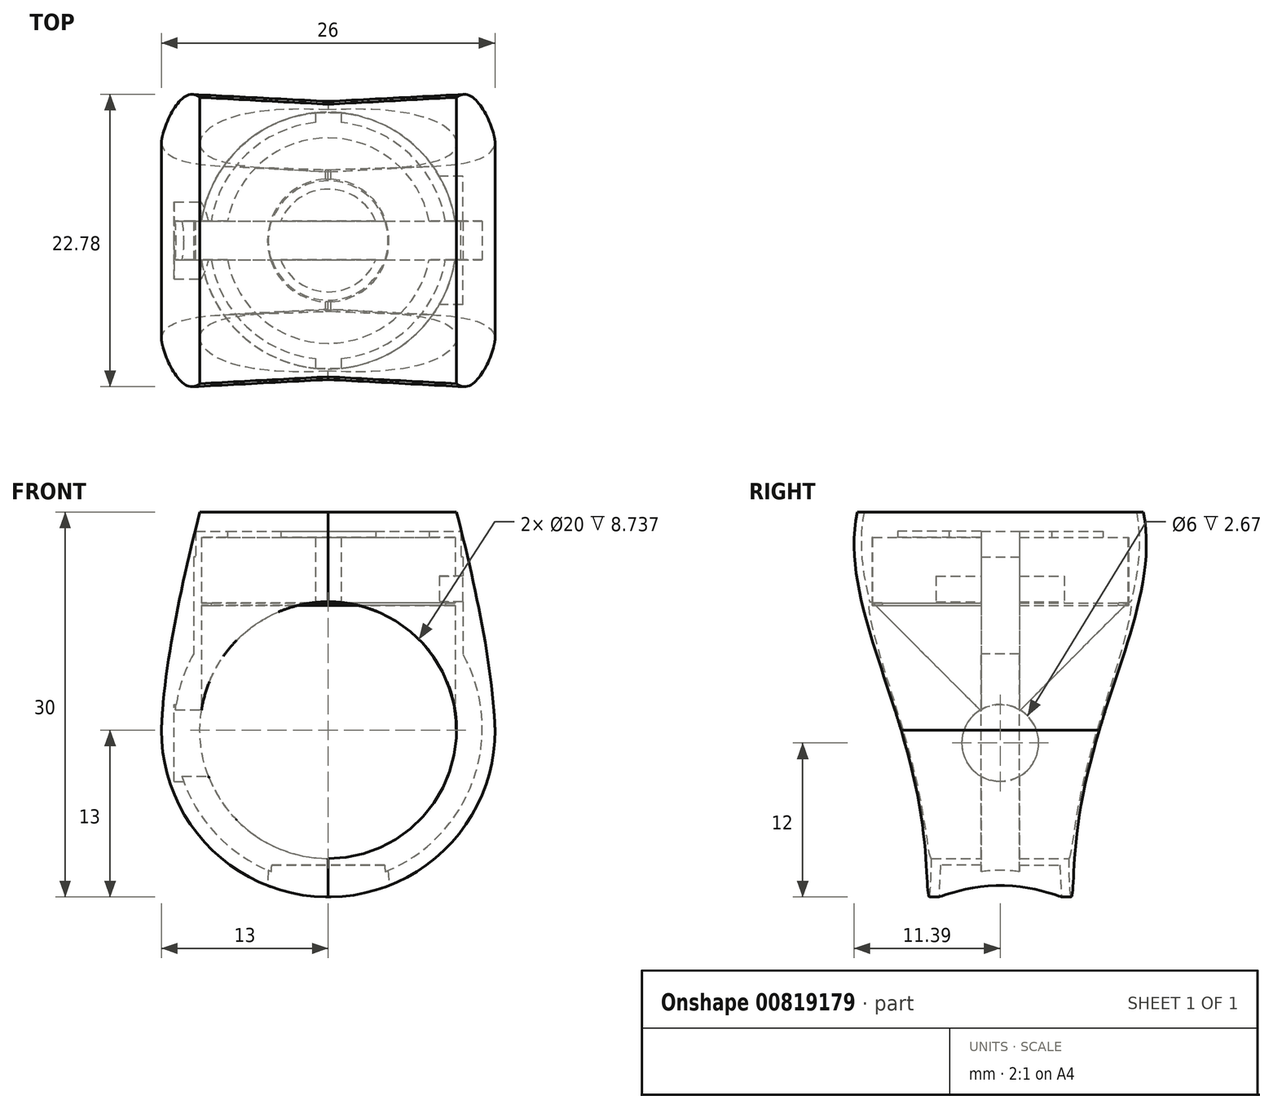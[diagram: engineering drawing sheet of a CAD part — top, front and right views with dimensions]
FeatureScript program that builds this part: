
annotation { "Feature Type Name" : "Feature", "Feature Type Description" : "" }
export const myFeature = defineFeature(function(context is Context, id is Id, definition is map)
    precondition{}
    {
        {
            var Q0;
            Q0=qCreatedBy(makeId("Front.planeOp"),FACE);
            var sketch = newSketch(context, id + "F0", { "sketchPlane" : qUnion([Q0])});
            skCircle(sketch, "E0", {"center": v(0, 0) * mm, "radius": 10 * mm});
            skLineSegment(sketch, "E1.bottom", {"start": v(-10, 11) * mm, "end": v(10, 11) * mm});
            skLineSegment(sketch, "E1.top", {"start": v(-10, 17) * mm, "end": v(10, 17) * mm});
            skLineSegment(sketch, "E1.left", {"start": v(-10, 11) * mm, "end": v(-10, 17) * mm});
            skLineSegment(sketch, "E1.right", {"start": v(10, 11) * mm, "end": v(10, 17) * mm});
            skPoint(sketch, "E1.middle", {"position": v(0, 14) * mm});
            skCircle(sketch, "E2.0", {"center": v(0, 0) * mm, "radius": 13 * mm});
            skPoint(sketch, "E3", {"position": v(0, 17) * mm});
            skPoint(sketch, "E4", {"position": v(0, 10) * mm});
            skFitSpline(sketch, "E5", {"points": [v(-10, 17) * mm, v(-13, 0) * mm], "startDerivative": vector(-4.4, -17) * mm, "endDerivative": vector(-0.5, -14.41) * mm});
            skFitSpline(sketch, "E6", {"points": [v(10, 17) * mm, v(13, 0) * mm], "startDerivative": vector(4.4, -17) * mm, "endDerivative": vector(0.5, -14.41) * mm});
            skSolve(sketch);
        }
        {
            var Q0;
            Q0=makeQuery(id+"F0.imprint","IMPRINT",FACE,{"disambiguationData":[TD([[makeQuery(id+"F0.imprint","IMPRINT",EDGE,{"derivedFrom":sQuery(id+"F0.wireOp",EDGE,"E0")}),-1.0]])]});
            var Q1;
            {var subQ0=sQuery(id+"F0.wireOp",EDGE,"E1.left");Q1=makeQuery(id+"F0.imprint","IMPRINT",FACE,{"disambiguationData":[TD([[makeQuery(id+"F0.imprint","IMPRINT",EDGE,{"derivedFrom":subQ0}),1.0]])]});}
            var Q2;
            {var subQ0=sQuery(id+"F0.wireOp",EDGE,"E1.right");Q2=makeQuery(id+"F0.imprint","IMPRINT",FACE,{"disambiguationData":[TD([[makeQuery(id+"F0.imprint","IMPRINT",EDGE,{"derivedFrom":subQ0}),-1.0]])]});}
            var Q3;
            {var subQ0=sQuery(id+"F0.wireOp",EDGE,"E2.0");var subQ1=sQuery(id+"F0.wireOp",EDGE,"E1.bottom");var subQ2=makeQuery(id+"F0.imprint","INTERSECT",VERTEX,{"disambiguationData":[OD(0.0)],"derivedFrom":[subQ1,subQ0]});Q3=makeQuery(id+"F0.imprint","IMPRINT",FACE,{"disambiguationData":[TD([[makeQuery(id+"F0.imprint","IMPRINT",EDGE,{"disambiguationData":[TD([[subQ2,-1.0]])],"derivedFrom":subQ1}),1.0]])]});}
            var Q4;
            Q4=makeQuery(id+"F0.imprint","IMPRINT",FACE,{"disambiguationData":[TD([[makeQuery(id+"F0.imprint","IMPRINT",EDGE,{"derivedFrom":sQuery(id+"F0.wireOp",EDGE,"E1.top")}),-1.0]])]});
            extrude(context, id + "F1", {"entities" : qUnion([Q0, Q1, Q2, Q3, Q4]), "depth" : 24.5 * mm, "offsetDistance" : 25 * mm, "symmetric" : true});
        }
        {
            var Q0;
            Q0=qCreatedBy(makeId("Right.planeOp"),FACE);
            var sketch = newSketch(context, id + "F2", { "sketchPlane" : qUnion([Q0])});
            skFitSpline(sketch, "E7", {"points": [v(-10.5, 17.51) * mm, v(-5.5, -12.99) * mm], "startDerivative": vector(-6.24, -25.28) * mm, "endDerivative": vector(-3.92, -38.96) * mm});
            skFitSpline(sketch, "E8", {"points": [v(10.5, 17.51) * mm, v(5.5, -12.99) * mm], "startDerivative": vector(6.24, -25.28) * mm, "endDerivative": vector(3.92, -38.96) * mm});
            skLineSegment(sketch, "E9", {"start": v(-5.5, -12.99) * mm, "end": v(5.5, -12.99) * mm});
            skLineSegment(sketch, "E10", {"start": v(-10.5, 17.51) * mm, "end": v(10.5, 17.51) * mm});
            skSolve(sketch);
        }
        {
            var Q0;
            Q0=qCreatedBy(makeId("Top.planeOp"),FACE);
            var sketch = newSketch(context, id + "F3", { "sketchPlane" : qUnion([Q0])});
            skPoint(sketch, "E11", {"position": v(0, 0) * mm});
            skCircle(sketch, "E12", {"center": v(0, 0) * mm, "radius": 10 * mm});
            skSolve(sketch);
        }
        {
            var Q0;
            Q0 = qSketchRegion(id + "F2", true);
            extrude(context, id + "F4", {"entities" : qUnion([Q0]), "operationType" : NewBodyOperationType.INTERSECT, "oppositeDirection" : true, "depth" : 80 * mm, "offsetDistance" : 25 * mm, "hasDraft" : true, "draftAngle" : 3 * degree, "symmetric" : true});
        }
        {
            var Q0;
            Q0 = qSketchRegion(id + "F3", true);
            var Q1;
            Q1 = qSketchRegion(id + "F12", true);
            extrude(context, id + "F5", {"entities" : qUnion([Q0, Q1]), "operationType" : NewBodyOperationType.REMOVE, "depth" : 15 * mm, "offsetDistance" : 25 * mm});
        }
        {
            var Q0;
            Q0=qCreatedBy(makeId("Top.planeOp"),FACE);
            var sketch = newSketch(context, id + "F6", { "sketchPlane" : qUnion([Q0])});
            skCircle(sketch, "E13", {"center": v(0, 0) * mm, "radius": 4.1 * mm});
            skSolve(sketch);
        }
        {
            var Q0;
            Q0 = qSketchRegion(id + "F6", true);
            extrude(context, id + "F7", {"entities" : qUnion([Q0]), "operationType" : NewBodyOperationType.REMOVE, "oppositeDirection" : true, "depth" : 14.4 * mm, "offsetDistance" : 44 * mm, "hasDraft" : true, "draftAngle" : 3 * degree, "hasSecondDirection" : true, "secondDirectionOppositeDirection" : true, "secondDirectionDepth" : 10.5 * mm});
        }
        {
            var Q0;
            Q0=qCreatedBy(makeId("Front.planeOp"),FACE);
            var sketch = newSketch(context, id + "F8", { "sketchPlane" : qUnion([Q0])});
            skCircle(sketch, "E14", {"center": v(0, 0.13) * mm, "radius": 12 * mm});
            skSolve(sketch);
        }
        {
            var Q0;
            Q0 = qSketchRegion(id + "F8", true);
            extrude(context, id + "F9", {"entities" : qUnion([Q0]), "operationType" : NewBodyOperationType.REMOVE, "oppositeDirection" : true, "depth" : 3 * mm, "offsetDistance" : 25 * mm, "symmetric" : true});
        }
        {
            var Q0;
            Q0=qCreatedBy(makeId("Right.planeOp"),FACE);
            var sketch = newSketch(context, id + "F10", { "sketchPlane" : qUnion([Q0])});
            skLineSegment(sketch, "E15.bottom", {"start": v(-1.5, 12.05) * mm, "end": v(1.5, 12.05) * mm});
            skLineSegment(sketch, "E15.top", {"start": v(-1.5, 3.05) * mm, "end": v(1.5, 3.05) * mm});
            skLineSegment(sketch, "E15.left", {"start": v(-1.5, 12.05) * mm, "end": v(-1.5, 3.05) * mm});
            skLineSegment(sketch, "E15.right", {"start": v(1.5, 12.05) * mm, "end": v(1.5, 3.05) * mm});
            skPoint(sketch, "E15.middle", {"position": v(0, 7.55) * mm});
            skSolve(sketch);
        }
        {
            var Q0;
            Q0 = qSketchRegion(id + "F10", true);
            var Q1;
            Q1 = qSketchRegion(id + "F12", true);
            extrude(context, id + "F11", {"entities" : qUnion([Q0, Q1]), "operationType" : NewBodyOperationType.REMOVE, "oppositeDirection" : true, "depth" : 21 * mm, "offsetDistance" : 25 * mm, "symmetric" : true});
        }
        {
            var Q0;
            Q0=qCreatedBy(makeId("Top.planeOp"),FACE);
            var sketch = newSketch(context, id + "F12", { "sketchPlane" : qUnion([Q0])});
            skCircle(sketch, "E16", {"center": v(0, 0) * mm, "radius": 4 * mm});
            skCircle(sketch, "E17.0", {"center": v(0, 0) * mm, "radius": 8 * mm});
            skSolve(sketch);
        }
        {
            var Q0;
            Q0 = qSketchRegion(id + "F12", true);
            extrude(context, id + "F13", {"entities" : qUnion([Q0]), "operationType" : NewBodyOperationType.REMOVE, "depth" : 15.5 * mm, "offsetDistance" : 25 * mm});
        }
        {
            var Q0;
            Q0=qCreatedBy(makeId("Right.planeOp"),FACE);
            var sketch = newSketch(context, id + "F14", { "sketchPlane" : qUnion([Q0])});
            skCircle(sketch, "E18", {"center": v(0, -1) * mm, "radius": 3 * mm});
            skSolve(sketch);
        }
        {
            var Q0;
            Q0 = qSketchRegion(id + "F14", true);
            extrude(context, id + "F15", {"entities" : qUnion([Q0]), "operationType" : NewBodyOperationType.REMOVE, "oppositeDirection" : true, "depth" : 12 * mm, "offsetDistance" : 25 * mm});
        }
        {
            var Q0;
            Q0=qCreatedBy(makeId("Top.planeOp"),FACE);
            var sketch = newSketch(context, id + "F16", { "sketchPlane" : qUnion([Q0])});
            skLineSegment(sketch, "E19.bottom", {"start": v(-10.32, -1.5) * mm, "end": v(10.32, -1.5) * mm});
            skLineSegment(sketch, "E19.top", {"start": v(-10.32, 1.5) * mm, "end": v(10.32, 1.5) * mm});
            skLineSegment(sketch, "E19.left", {"start": v(-10.32, -1.5) * mm, "end": v(-10.32, 1.5) * mm});
            skLineSegment(sketch, "E19.right", {"start": v(10.32, -1.5) * mm, "end": v(10.32, 1.5) * mm});
            skPoint(sketch, "E19.middle", {"position": v(0, 0) * mm});
            skSolve(sketch);
        }
        {
            var Q0;
            Q0 = qSketchRegion(id + "F16", true);
            extrude(context, id + "F17", {"entities" : qUnion([Q0]), "operationType" : NewBodyOperationType.REMOVE, "depth" : 15.5 * mm, "offsetDistance" : 25 * mm});
        }
        {
            var Q0;
            Q0=qCreatedBy(makeId("Right.planeOp"),FACE);
            var sketch = newSketch(context, id + "F18", { "sketchPlane" : qUnion([Q0])});
            skLineSegment(sketch, "E20.bottom", {"start": v(-5, 10) * mm, "end": v(5, 10) * mm});
            skLineSegment(sketch, "E20.top", {"start": v(-5, 12) * mm, "end": v(5, 12) * mm});
            skLineSegment(sketch, "E20.left", {"start": v(-5, 10) * mm, "end": v(-5, 12) * mm});
            skLineSegment(sketch, "E20.right", {"start": v(5, 10) * mm, "end": v(5, 12) * mm});
            skPoint(sketch, "E20.middle", {"position": v(0, 11) * mm});
            skSolve(sketch);
        }
        {
            var Q0;
            Q0 = qSketchRegion(id + "F18", true);
            extrude(context, id + "F19", {"entities" : qUnion([Q0]), "operationType" : NewBodyOperationType.REMOVE, "depth" : 10.5 * mm, "offsetDistance" : 25 * mm});
        }
        {
            var Q0;
            Q0=qCreatedBy(makeId("Top.planeOp"),FACE);
            var sketch = newSketch(context, id + "F20", { "sketchPlane" : qUnion([Q0])});
            skCircle(sketch, "E21", {"center": v(0, 0) * mm, "radius": 10 * mm});
            skCircle(sketch, "E22.0", {"center": v(0, 0) * mm, "radius": 9.25 * mm});
            skSolve(sketch);
        }
        {
            var Q0;
            Q0 = qSketchRegion(id + "F20", true);
            extrude(context, id + "F21", {"entities" : qUnion([Q0]), "operationType" : NewBodyOperationType.ADD, "depth" : 9.9 * mm, "offsetDistance" : 25 * mm, "hasSecondDirection" : true, "secondDirectionOppositeDirection" : false, "secondDirectionDepth" : 9.7 * mm});
        }
        {
            var Q0;
            Q0=qCreatedBy(makeId("Right.planeOp"),FACE);
            var sketch = newSketch(context, id + "F22", { "sketchPlane" : qUnion([Q0])});
            skLineSegment(sketch, "E23.bottom", {"start": v(-1.5, 8.48) * mm, "end": v(1.5, 8.48) * mm});
            skLineSegment(sketch, "E23.top", {"start": v(-1.5, 13.48) * mm, "end": v(1.5, 13.48) * mm});
            skLineSegment(sketch, "E23.left", {"start": v(-1.5, 8.48) * mm, "end": v(-1.5, 13.48) * mm});
            skLineSegment(sketch, "E23.right", {"start": v(1.5, 8.48) * mm, "end": v(1.5, 13.48) * mm});
            skPoint(sketch, "E23.middle", {"position": v(0, 10.98) * mm});
            skSolve(sketch);
        }
        {
            var Q0;
            Q0 = qSketchRegion(id + "F22", true);
            extrude(context, id + "F23", {"entities" : qUnion([Q0]), "operationType" : NewBodyOperationType.REMOVE, "depth" : 21 * mm, "offsetDistance" : 25 * mm, "symmetric" : true});
        }
        {
            var Q0;
            Q0=qCreatedBy(makeId("Top.planeOp"),FACE);
            var sketch = newSketch(context, id + "F24", { "sketchPlane" : qUnion([Q0])});
            skLineSegment(sketch, "E24.bottom", {"start": v(1, -9.95) * mm, "end": v(-1, -9.95) * mm});
            skLineSegment(sketch, "E24.top", {"start": v(1, 9.95) * mm, "end": v(-1, 9.95) * mm});
            skLineSegment(sketch, "E24.left", {"start": v(1, -9.95) * mm, "end": v(1, 9.95) * mm});
            skLineSegment(sketch, "E24.right", {"start": v(-1, -9.95) * mm, "end": v(-1, 9.95) * mm});
            skPoint(sketch, "E24.middle", {"position": v(0, 0) * mm});
            skSolve(sketch);
        }
        {
            var Q0;
            Q0 = qSketchRegion(id + "F24", true);
            extrude(context, id + "F25", {"entities" : qUnion([Q0]), "operationType" : NewBodyOperationType.REMOVE, "depth" : 15 * mm, "offsetDistance" : 25 * mm});
        }
    });
